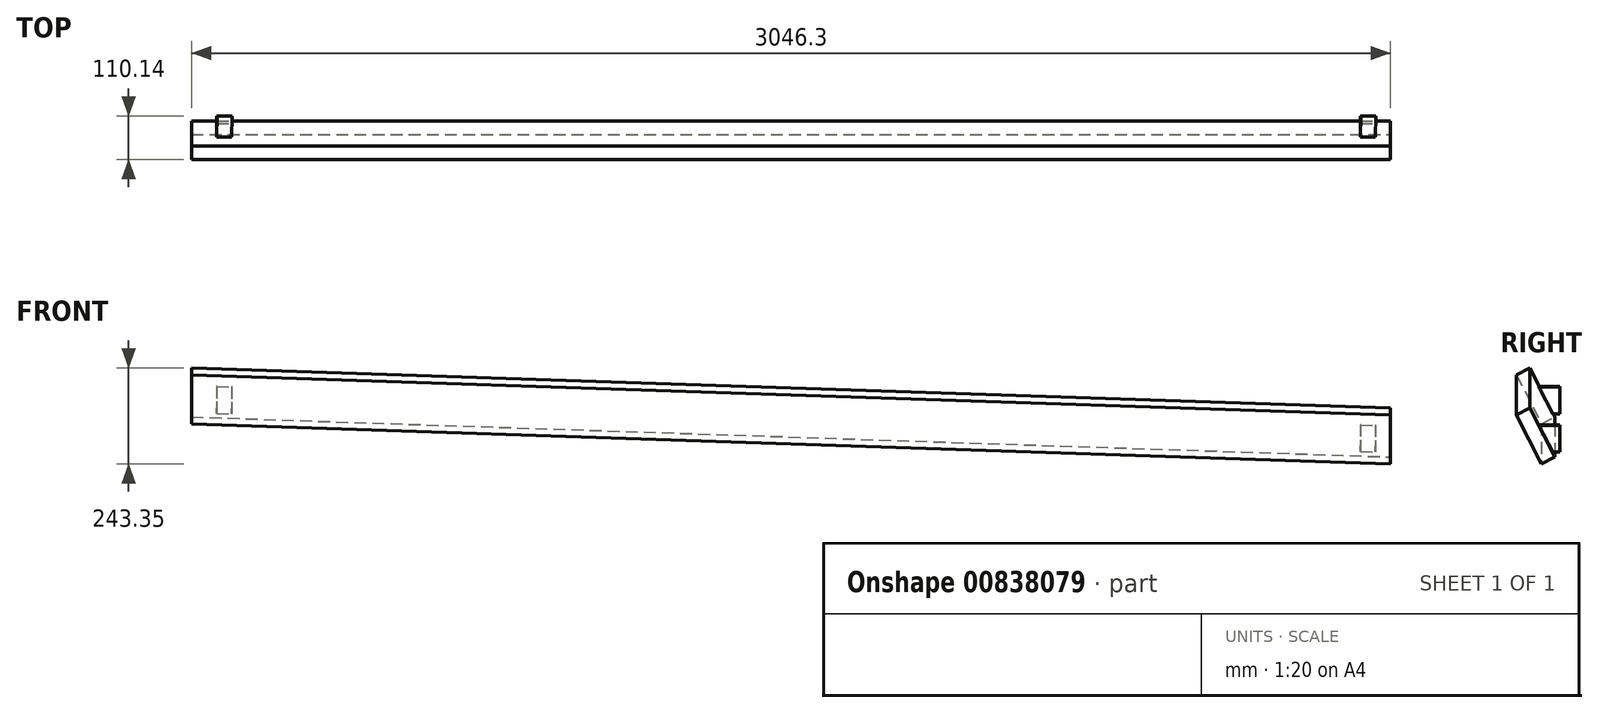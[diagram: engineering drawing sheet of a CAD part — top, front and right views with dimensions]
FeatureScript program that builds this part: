
annotation { "Feature Type Name" : "Feature", "Feature Type Description" : "" }
export const myFeature = defineFeature(function(context is Context, id is Id, definition is map)
    precondition{}
    {
        {
            var Q0;
            Q0=qCreatedBy(makeId("Front.planeOp"),FACE);
            var sketch = newSketch(context, id + "F0", { "sketchPlane" : qUnion([Q0])});
            skLineSegment(sketch, "E0", {"start": v(-129.81, 1016) * mm, "end": v(2916.5, 914.4) * mm});
            skLineSegment(sketch, "E1", {"start": v(-126.67, 0) * mm, "end": v(169.12, 0) * mm, "construction": true});
            skSolve(sketch);
        }
        {
            var Q0;
            Q0=qCreatedBy(makeId("Right.planeOp"),FACE);
            var sketch = newSketch(context, id + "F1", { "sketchPlane" : qUnion([Q0])});
            skLineSegment(sketch, "E2", {"start": v(-76.2, 1016) * mm, "end": v(-110.14, 998.68) * mm});
            skLineSegment(sketch, "E3", {"start": v(-110.14, 998.68) * mm, "end": v(-46.64, 874.25) * mm});
            skLineSegment(sketch, "E4", {"start": v(-46.64, 874.25) * mm, "end": v(-12.7, 891.57) * mm});
            skLineSegment(sketch, "E5", {"start": v(-12.7, 891.57) * mm, "end": v(-76.2, 1016) * mm});
            skPoint(sketch, "E6", {"position": v(-53.1, 970.75) * mm});
            skLineSegment(sketch, "E7", {"start": v(0, 812.8) * mm, "end": v(0, 0) * mm, "construction": true});
            skPoint(sketch, "E8", {"position": v(-18.47, 902.88) * mm});
            skSolve(sketch);
        }
        {
            var Q0;
            Q0=makeQuery(id+"F1.imprint","IMPRINT",FACE,{"disambiguationData":[TD([[makeQuery(id+"F1.imprint","IMPRINT",EDGE,{"derivedFrom":sQuery(id+"F1.wireOp",EDGE,"E2")}),1.0]])]});
            var Q1;
            Q1=sQuery(id+"F0.wireOp",EDGE,"E0");
            sweep(context, id + "F2", {"profiles" : qUnion([Q0]), "path" : qUnion([Q1]), "keepProfileOrientation" : true});
        }
        {
            var Q0;
            Q0=qCreatedBy(makeId("Right.planeOp"),FACE);
            var sketch = newSketch(context, id + "F3", { "sketchPlane" : qUnion([Q0])});
            skLineSegment(sketch, "E9", {"start": v(-53.1, 970.75) * mm, "end": v(0, 970.75) * mm});
            skLineSegment(sketch, "E10", {"start": v(0, 970.75) * mm, "end": v(0, 902.88) * mm});
            skLineSegment(sketch, "E11", {"start": v(0, 902.88) * mm, "end": v(-18.47, 902.88) * mm});
            skLineSegment(sketch, "E12", {"start": v(-18.47, 902.88) * mm, "end": v(-53.1, 970.75) * mm});
            skSolve(sketch);
        }
        {
            var Q0;
            Q0 = qSketchRegion(id + "F3", true);
            var Q1;
            Q1=sQuery(id+"F0.wireOp",EDGE,"E0");
            sweep(context, id + "F4", {"profiles" : qUnion([Q0]), "path" : qUnion([Q1])});
        }
        {
            var Q0;
            Q0=makeQuery(id+"F2.opSweep","SWEPT_FACE",FACE,{"disambiguationData":[OSD([sQuery(id+"F0.wireOp",EDGE,"E0"),sQuery(id+"F1.wireOp",EDGE,"E5")])]});
            var sketch = newSketch(context, id + "F5", { "sketchPlane" : qUnion([Q0])});
            skLineSegment(sketch, "E13.bottom", {"start": v(-2872.4, 854.11) * mm, "end": v(-2931.4, 854.11) * mm});
            skLineSegment(sketch, "E13.top", {"start": v(-2872.4, 600.11) * mm, "end": v(-2931.4, 600.11) * mm});
            skLineSegment(sketch, "E13.left", {"start": v(-2872.4, 854.11) * mm, "end": v(-2872.4, 600.11) * mm});
            skLineSegment(sketch, "E13.right", {"start": v(-2931.4, 854.11) * mm, "end": v(-2931.4, 600.11) * mm});
            skLineSegment(sketch, "E14.bottom", {"start": v(-953.2, 970.56) * mm, "end": v(-1936.98, 970.56) * mm});
            skLineSegment(sketch, "E14.top", {"start": v(-953.2, 705.1) * mm, "end": v(-1936.98, 705.1) * mm});
            skLineSegment(sketch, "E15.bottom", {"start": v(-1936.98, 970.56) * mm, "end": v(-2834.3, 970.56) * mm});
            skLineSegment(sketch, "E15.top", {"start": v(-1936.98, 698.63) * mm, "end": v(-2834.3, 698.63) * mm});
            skLineSegment(sketch, "E15.left", {"start": v(-1936.98, 705.1) * mm, "end": v(-1936.98, 698.63) * mm});
            skLineSegment(sketch, "E15.right", {"start": v(-2834.3, 970.56) * mm, "end": v(-2834.3, 698.63) * mm});
            skLineSegment(sketch, "E16.bottom", {"start": v(71.78, 1090.12) * mm, "end": v(348.22, 1090.12) * mm});
            skLineSegment(sketch, "E16.top", {"start": v(71.78, 625.7) * mm, "end": v(348.22, 625.7) * mm});
            skLineSegment(sketch, "E16.left", {"start": v(71.78, 1090.12) * mm, "end": v(71.78, 625.7) * mm});
            skLineSegment(sketch, "E16.right", {"start": v(348.22, 1090.12) * mm, "end": v(348.22, 625.7) * mm});
            skLineSegment(sketch, "E17.bottom", {"start": v(-953.2, 1159.23) * mm, "end": v(33.68, 1159.23) * mm});
            skLineSegment(sketch, "E17.top", {"start": v(-953.2, 421.14) * mm, "end": v(33.68, 421.14) * mm});
            skLineSegment(sketch, "E17.left", {"start": v(-953.2, 1159.23) * mm, "end": v(-953.2, 970.56) * mm});
            skLineSegment(sketch, "E17.right", {"start": v(33.68, 1159.23) * mm, "end": v(33.68, 421.14) * mm});
            skLineSegment(sketch, "E18.trimOffspring", {"start": v(-953.2, 705.1) * mm, "end": v(-953.2, 421.14) * mm});
            skSolve(sketch);
        }
        {
            var Q0;
            Q0 = qSketchRegion(id + "F5", true);
            extrude(context, id + "F6", {"entities" : qUnion([Q0]), "operationType" : NewBodyOperationType.REMOVE, "depth" : 127 * mm, "offsetDistance" : 25.4 * mm});
        }
    });
